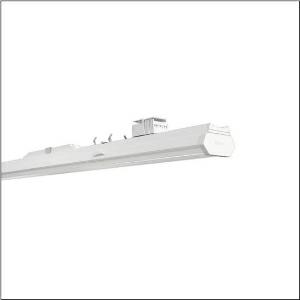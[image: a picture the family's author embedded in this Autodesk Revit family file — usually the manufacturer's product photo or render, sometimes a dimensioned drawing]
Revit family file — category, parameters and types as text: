
# Revit family: licross_r__11_protected_ho_51ts11vn4dxr_b2c4
name_source: partatom
category: Lighting Fixtures
units: mm (PartAtom-declared; Revit-internal decimal feet)

## family parameters
Cut with Voids When Loaded = No
Host = Face
Light Source = No
Part Type = Normal
Room Calculation Point = No
Round Connector Dimension = Use Diameter
Shared = No

## types (1)
- --- (1 x LED, 13190 lm, 77.9 W, 4000K)
    Apparent Load = 78 VA
    CIE Flux Codes = 84 94 98 99 100
    Color Rendering = 80
    Color Temperature = 4000K
    Default Elevation = 1800 mm
    Description = Licross® 11 Protected HO, luminaire insert, of sheet steel, galvanised, coil coated, white, length: 1.500mm, width: 90mm, height: 101mm, LED rated luminous flux: 13.190lm, light colour: 840, control gear: DALI 2, CLO, control gear: ECG DALI, with plug, 5-pole, with phase selection, mains connection: 220..240V, AC, 50/60Hz, halogen-free wiring, primary optical cover: cover, of PMMA, light emission: direct with ceiling illumination distribution, protection rating (complete): IP50, insulation class (complete): insulation class I (protective earthing), certification: CE, ENEC, VDE, UKCA, protection symbol: D if used in an environment with non-conductive dust loads with corresponding accessories, permissible ambient temperature for indoor applications: -25..+35°C, corresponds to IFS (International Featured Standards) requirements for safety and quality in the food industry, reducing of maximum allowable ambient temperature of 5°C with ceiling mounting, LABS conformity tested according to VDMA 24364:2018-05, packaging unit: 1 piece
    Height = 92 mm
    Lamp = 1 x LED
    Lamp Light Flux = 13190 lm
    Lamp Power = 77.9 W
    Lamp count = 1
    Length = 1500 mm
    Luminous efficacy = 169 lm/W
    Manufacturer = Siteco
    ModVariant = No
    Model = 51TS11VN4DXR
    Mounting Place = Ceiling
    Mounting Type = Pendant
    Number of Poles = 1
    OnlyDefault = Yes
    Power Factor = 1
    Product Name = Licross® 11 Protected HO
    Product group = luminaire insert
    ProductGroupID = 902
    Protection Class = Protection class I
    Protection Degree = IP 50
    RLX_Detail_Level = 1
    RlxData = <blob elided: 24293 chars, md5=c1663d49>
    Socket = socket
    Standby Power = 0 W
    System Light Flux = 13190 lm
    System Power = 78 W
    Type Comments = factory setting: luminous flux: 100 % | dim-lin: 254 | 440 mA
    Type Image = l_1256145.jpg
    URL = http://relux.com
    VarID = @adj_120929
    Voltage = 0 V
    Weight = 0.00 kg
    Width = 88 mm

## geometry (parser evidence)
native form markers: Blend x4, Sweep x12
no freeform markers — native parametric forms only
